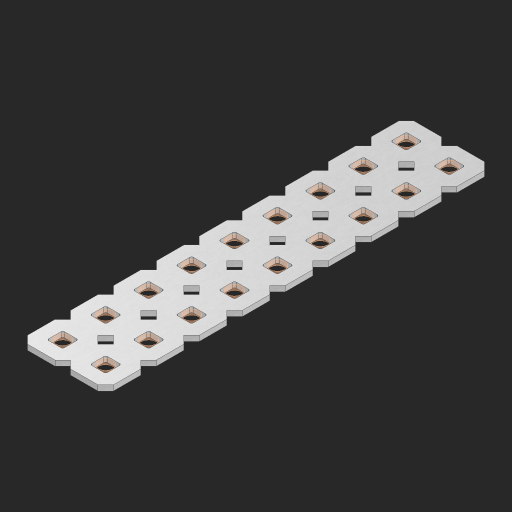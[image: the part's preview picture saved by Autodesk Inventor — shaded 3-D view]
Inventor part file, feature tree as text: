
AUTODESK INVENTOR PART (.ipt)
format: ipt  version: 2023 (Build 270158000, 158)  size: 484,864 bytes
history: native  units: in
note: dims shown in document units (in); Inventor stores cm internally (conversion verified against a paired STEP export)
features: other x19, extrude x17, sketch x2, pattern_linear x1
ambient origin geometry x8: Origin, YZ Plane, XZ Plane, XY Plane, X Axis, Y Axis, Z Axis, Center Point
bodies: Solid1 (feature_tree), Body (feature_tree)
feature tree (39):
  pattern_linear  "Rectangular Pattern1"  Spacing1=0.09in  [1 undecoded]
  sketch  "Sketch1"  dims[d1=0.5in]
  sketch  "Sketch2"  dims[d2=0.182in d3=0.09in d4=0.09in d5=0.09in d6=0.09in d7=0.09in d8=0.09in d9=0.09in d10=0.09in d11=0.02in d13=0.0in d14=0.172in d15=0.0625in d16=0.0in d19=0.5in d22=0.5in]
  other  "Srf1"
  other  "Srf126"
  other  "Srf127"
  other  "Srf128"
  other  "Srf129"
  other  "Srf130"
  other  "Srf131"
  other  "Srf250"
  other  "Srf251"
  other  "Srf268"
  other  "Srf269"
  other  "Srf270"
  other  "Srf271"
  other  "Srf272"
  other  "Srf273"
  other  "Srf274"
  other  "Srf275"
  other  "Srf276"
  other  "Circle"
  extrude  "ExtrusionSrf126"  Depth=0.09in
  extrude  "ExtrusionSrf127"  Depth=0.09in
  extrude  "ExtrusionSrf128"  Depth=0.09in
  extrude  "ExtrusionSrf129"  Depth=0.09in
  extrude  "ExtrusionSrf130"  Depth=0.09in
  extrude  "ExtrusionSrf131"  Depth=0.09in
  extrude  "ExtrusionSrf250"  Depth=0.09in
  extrude  "ExtrusionSrf251"  Depth=0.02in
  extrude  "ExtrusionSrf268"  TaperAngle=0.0deg  [1 undecoded]
  extrude  "ExtrusionSrf269"  Depth=0.5in
  extrude  "ExtrusionSrf270"  Depth=0.0625in TaperAngle=0.0deg
  extrude  "ExtrusionSrf271"  Depth=0.5in
  extrude  "ExtrusionSrf272"  Depth=0.5in
  extrude  "ExtrusionSrf273"  [1 undecoded]
  extrude  "ExtrusionSrf274"  [1 undecoded]
  extrude  "ExtrusionSrf275"  [1 undecoded]
  extrude  "ExtrusionSrf276"  [1 undecoded]
note: 6 required parameter values undecoded (feature->parameter linkage not recoverable at this tier; creation-order binding heuristic only, values carry confidence <= 0.55)
